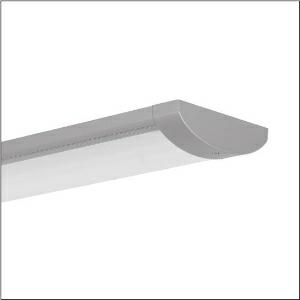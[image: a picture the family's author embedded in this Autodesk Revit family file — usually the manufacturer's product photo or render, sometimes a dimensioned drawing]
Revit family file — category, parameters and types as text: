
# Revit family: tv_20_5xa86172n0a
name_source: partatom
category: Lighting Fixtures
units: mm (PartAtom-declared; Revit-internal decimal feet)

## family parameters
Cut with Voids When Loaded = No
Host = Face
Light Source = No
Part Type = Normal
Room Calculation Point = No
Round Connector Dimension = Use Diameter
Shared = No

## types (1)
- TV 20 (1 x LED 4000K / CRI = 80 (unbekannt), 2130 lm, 4000K)
    Apparent Load = 21 VA
    CIE Flux Codes = 48 78 95 99 100
    Color Rendering = 80
    Color Temperature = 4000K
    Default Elevation = 1800 mm
    Description = TV 20, vandal-proof luminaire, primary light control with specular reflector, of aluminium, matt, primary optical cover: enclosure, of PC, frosted, light emission: direct distribution, primary light characteristic: symmetric, installation type: surface-mounted, LED, rated luminous flux: 2.130lm, luminous efficacy: 101lm/W, light colour: 840, colour temperature: 4000K, control gear: ON/OFF, mains connection: 230V, AC, 50Hz, rated input power: 21W, luminaire housing, of aluminium, coated, Siteco® metallic grey (DB 702S), with wall and ceiling fixing element, length: 705mm, width: 260mm, height: 70mm, mounting height: 2.5..4.0m, protection rating (complete): IP65, insulation class (complete): insulation class I (protective earthing), certification: CE, protection symbol: F, impact resistance: 2x IK10, standard: EN 60598, packaging unit: 1 piece
    Height = 70 mm
    Lamp = 1 x LED 4000K / CRI >= 80 (unbekannt)
    Lamp Light Flux = 2130 lm
    Lamp count = 1
    Length = 705 mm
    Luminous efficacy = 101 lm/W
    Manufacturer = Siteco
    ModVariant = No
    Model = 5XA86172N0A
    Mounting Place = Ceiling
    Mounting Type = Surface mounted
    Number of Poles = 1
    OnlyDefault = Yes
    Power Factor = 1
    Product Name = TV 20
    Product group = vandal-proof luminaire
    ProductGroupID = 310
    Protection Class = Protection class I
    Protection Degree = IP 65
    RLX_Detail_Level = 1
    RLX_Emergency_Light_Flux = 0 lm
    RLX_Emergency_Type = 0
    RLX_Emergency_Type_DB = No
    RlxData = <blob elided: 34145 chars, md5=b49089b4>
    Socket = socket
    Standby Power = 0 W
    System Light Flux = 2130 lm
    System Power = 21 W
    Type Comments = Product without accessories
    Type Image = l_1004809.jpg
    URL = http://relux.com
    VarID = ---
    Voltage = 0 V
    Weight = 0.00 kg
    Width = 260 mm

## geometry (parser evidence)
native form markers: Blend x4, Sweep x11
no freeform markers — native parametric forms only
